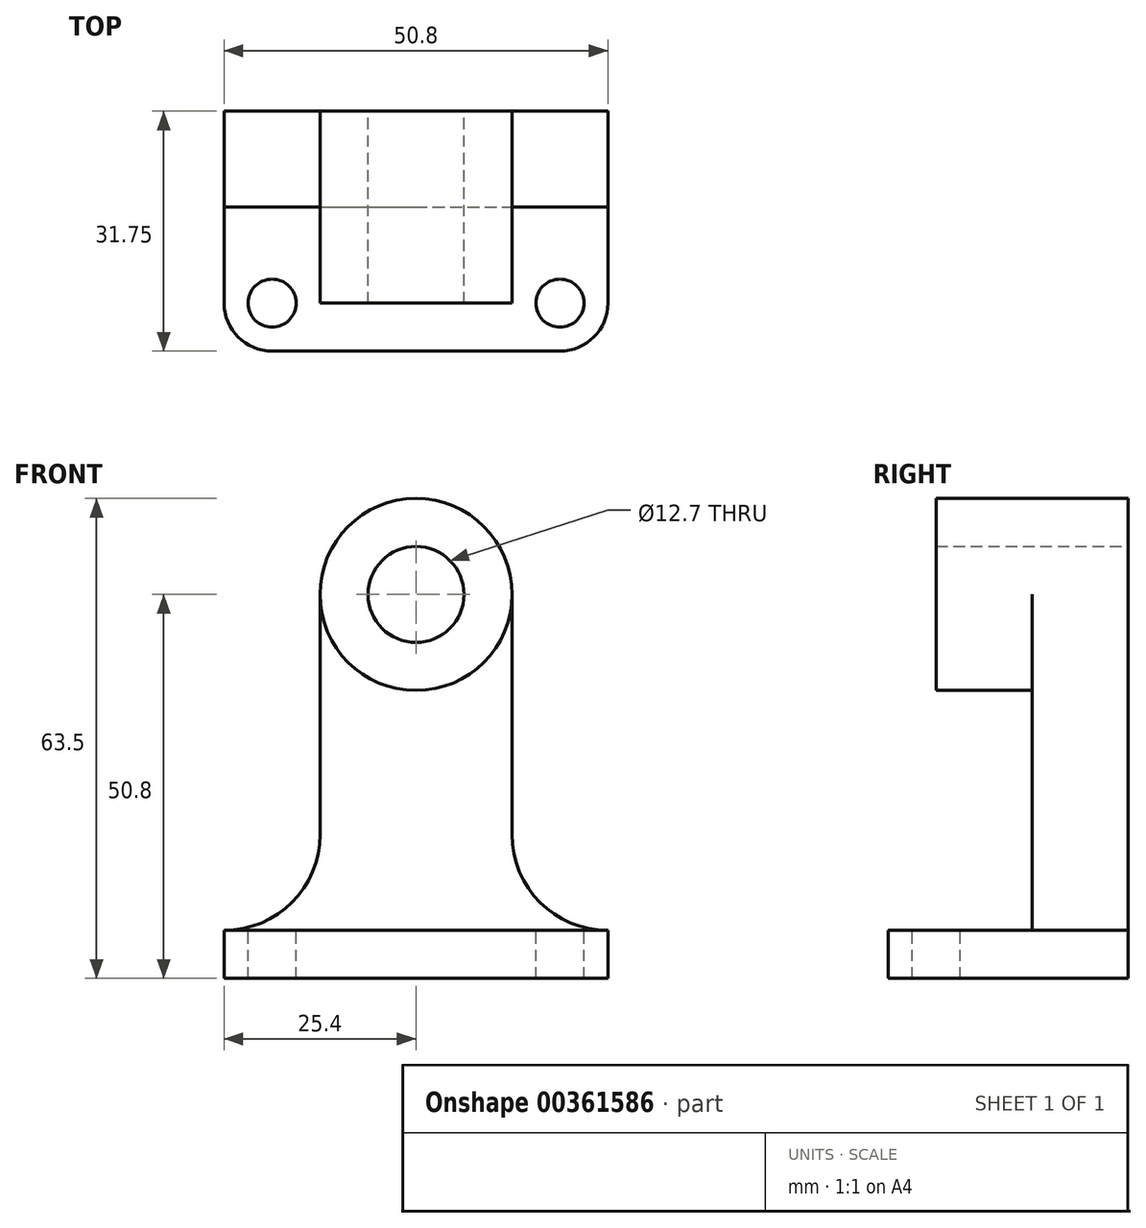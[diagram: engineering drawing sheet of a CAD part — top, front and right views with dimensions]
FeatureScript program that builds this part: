
annotation { "Feature Type Name" : "Feature", "Feature Type Description" : "" }
export const myFeature = defineFeature(function(context is Context, id is Id, definition is map)
    precondition{}
    {
        {
            var Q0;
            Q0=qCreatedBy(makeId("Front.planeOp"),FACE);
            var sketch = newSketch(context, id + "F0", { "sketchPlane" : qUnion([Q0])});
            skLineSegment(sketch, "E0", {"start": v(0, 0) * mm, "end": v(50.8, 0) * mm});
            skLineSegment(sketch, "E1", {"start": v(50.8, 0) * mm, "end": v(50.8, 63.5) * mm});
            skLineSegment(sketch, "E2", {"start": v(50.8, 63.5) * mm, "end": v(0, 63.5) * mm});
            skLineSegment(sketch, "E3", {"start": v(0, 63.5) * mm, "end": v(0, 0) * mm});
            skSolve(sketch);
        }
        {
            var Q0;
            Q0=makeQuery(id+"F0.imprint","IMPRINT",FACE,{"disambiguationData":[TD([[makeQuery(id+"F0.imprint","IMPRINT",EDGE,{"derivedFrom":sQuery(id+"F0.wireOp",EDGE,"E0")}),1.0]])]});
            extrude(context, id + "F1", {"entities" : qUnion([Q0]), "depth" : 31.75 * mm});
        }
        {
            var Q0;
            Q0=makeQuery(id+"F1.opExtrude","CAP_FACE",FACE,{"disambiguationData":[OSD([sQuery(id+"F0.wireOp",EDGE,"E0"),sQuery(id+"F0.wireOp",EDGE,"E1"),sQuery(id+"F0.wireOp",EDGE,"E2"),sQuery(id+"F0.wireOp",EDGE,"E3")])],"isStart":false});
            var sketch = newSketch(context, id + "F2", { "sketchPlane" : qUnion([Q0])});
            skLineSegment(sketch, "E4", {"start": v(0, 6.35) * mm, "end": v(50.8, 6.35) * mm});
            skLineSegment(sketch, "E5", {"start": v(12.7, 6.35) * mm, "end": v(12.7, 63.5) * mm});
            skLineSegment(sketch, "E6", {"start": v(12.7, 63.5) * mm, "end": v(38.1, 63.5) * mm});
            skLineSegment(sketch, "E7", {"start": v(38.1, 63.5) * mm, "end": v(38.1, 6.35) * mm});
            skLineSegment(sketch, "E8", {"start": v(12.7, 38.1) * mm, "end": v(38.1, 38.1) * mm});
            skSolve(sketch);
        }
        {
            var Q0;
            {var subQ4=makeQuery(id+"F1.opExtrude","CAP_EDGE",EDGE,{"disambiguationData":[OSD([sQuery(id+"F0.wireOp",EDGE,"E3")])],"isStart":false});var subQ6=sQuery(id+"F2.wireOp",EDGE,"E4");var subQ7=makeQuery(id+"F2.imprint","INTERSECT",VERTEX,{"derivedFrom":[subQ4,subQ6]});Q0=makeQuery(id+"F2.imprint","IMPRINT",FACE,{"disambiguationData":[TD([[makeQuery(id+"F2.imprint","IMPRINT",EDGE,{"disambiguationData":[TD([[subQ7,-1.0]])],"derivedFrom":subQ6}),1.0]])]});}
            var Q1;
            {var subQ5=sQuery(id+"F2.wireOp",EDGE,"E8");Q1=makeQuery(id+"F2.imprint","IMPRINT",FACE,{"disambiguationData":[TD([[makeQuery(id+"F2.imprint","IMPRINT",EDGE,{"derivedFrom":subQ5}),-1.0]])]});}
            var Q2;
            {var subQ1=makeQuery(id+"F1.opExtrude","CAP_EDGE",EDGE,{"disambiguationData":[OSD([sQuery(id+"F0.wireOp",EDGE,"E1")])],"isStart":false});var subQ3=sQuery(id+"F2.wireOp",EDGE,"E4");var subQ4=makeQuery(id+"F2.imprint","INTERSECT",VERTEX,{"derivedFrom":[subQ1,subQ3]});Q2=makeQuery(id+"F2.imprint","IMPRINT",FACE,{"disambiguationData":[TD([[makeQuery(id+"F2.imprint","IMPRINT",EDGE,{"disambiguationData":[TD([[subQ4,1.0]])],"derivedFrom":subQ3}),1.0]])]});}
            extrude(context, id + "F3", {"entities" : qUnion([Q0, Q1, Q2]), "operationType" : NewBodyOperationType.REMOVE, "oppositeDirection" : true, "depth" : 19.05 * mm});
        }
        {
            var Q0;
            {var subQ0=sQuery(id+"F0.wireOp",EDGE,"E2");Q0=makeQuery(id+"F3.boolean.opBoolean","SPLIT",FACE,{"disambiguationData":[TD([makeQuery(id+"F1.opExtrude","SWEPT_FACE",FACE,{"disambiguationData":[OSD([subQ0])]})])],"derivedFrom":makeQuery(id+"F1.opExtrude","CAP_FACE",FACE,{"disambiguationData":[OSD([sQuery(id+"F0.wireOp",EDGE,"E0"),sQuery(id+"F0.wireOp",EDGE,"E1"),subQ0,sQuery(id+"F0.wireOp",EDGE,"E3")])],"isStart":false})});}
            var sketch = newSketch(context, id + "F4", { "sketchPlane" : qUnion([Q0])});
            skCircle(sketch, "E9", {"center": v(25.4, 50.8) * mm, "radius": 12.7 * mm});
            skPoint(sketch, "E9.centerSnap0", {"position": v(38.1, 50.8) * mm});
            skSolve(sketch);
        }
        {
            var Q0;
            {var subQ0=sQuery(id+"F4.wireOp",EDGE,"E9");var subQ1=makeQuery(id+"F1.opExtrude","CAP_EDGE",EDGE,{"disambiguationData":[OSD([sQuery(id+"F0.wireOp",EDGE,"E2")])],"isStart":false});var subQ2=makeQuery(id+"F4.imprint","INTERSECT",VERTEX,{"derivedFrom":[subQ1,subQ0]});Q0=makeQuery(id+"F4.imprint","IMPRINT",FACE,{"disambiguationData":[TD([[makeQuery(id+"F4.imprint","IMPRINT",EDGE,{"disambiguationData":[TD([[subQ2,-1.0]])],"derivedFrom":subQ0}),-1.0]])]});}
            var Q1;
            {var subQ0=sQuery(id+"F4.wireOp",EDGE,"E9");var subQ1=makeQuery(id+"F1.opExtrude","CAP_EDGE",EDGE,{"disambiguationData":[OSD([sQuery(id+"F0.wireOp",EDGE,"E2")])],"isStart":false});var subQ2=makeQuery(id+"F4.imprint","INTERSECT",VERTEX,{"derivedFrom":[subQ1,subQ0]});Q1=makeQuery(id+"F4.imprint","IMPRINT",FACE,{"disambiguationData":[TD([[makeQuery(id+"F4.imprint","IMPRINT",EDGE,{"disambiguationData":[TD([[subQ2,1.0]])],"derivedFrom":subQ0}),-1.0]])]});}
            var Q2;
            {var subQ0=sQuery(id+"F4.wireOp",EDGE,"E9");var subQ1=makeQuery(id+"F3.boolean.opBoolean","COPY",EDGE,{"derivedFrom":makeQuery(id+"F3.opExtrude","CAP_EDGE",EDGE,{"disambiguationData":[OSD([sQuery(id+"F2.wireOp",EDGE,"E5")])],"isStart":true})});var subQ2=makeQuery(id+"F4.imprint","INTERSECT",VERTEX,{"derivedFrom":[subQ1,subQ0]});Q2=makeQuery(id+"F4.imprint","IMPRINT",FACE,{"disambiguationData":[TD([[makeQuery(id+"F4.imprint","IMPRINT",EDGE,{"disambiguationData":[TD([[subQ2,-1.0]])],"derivedFrom":subQ0}),-1.0]])]});}
            var Q3;
            {var subQ0=sQuery(id+"F4.wireOp",EDGE,"E9");var subQ1=makeQuery(id+"F3.boolean.opBoolean","COPY",EDGE,{"derivedFrom":makeQuery(id+"F3.opExtrude","CAP_EDGE",EDGE,{"disambiguationData":[OSD([sQuery(id+"F2.wireOp",EDGE,"E7")])],"isStart":true})});var subQ2=makeQuery(id+"F4.imprint","INTERSECT",VERTEX,{"derivedFrom":[subQ1,subQ0]});Q3=makeQuery(id+"F4.imprint","IMPRINT",FACE,{"disambiguationData":[TD([[makeQuery(id+"F4.imprint","IMPRINT",EDGE,{"disambiguationData":[TD([[subQ2,1.0]])],"derivedFrom":subQ0}),-1.0]])]});}
            extrude(context, id + "F5", {"entities" : qUnion([Q0, Q1, Q2, Q3]), "operationType" : NewBodyOperationType.REMOVE, "oppositeDirection" : true, "depth" : 19.05 * mm});
        }
        {
            var Q0;
            {var subQ0=sQuery(id+"F0.wireOp",EDGE,"E2");Q0=makeQuery(id+"F3.boolean.opBoolean","SPLIT",FACE,{"disambiguationData":[TD([makeQuery(id+"F1.opExtrude","SWEPT_FACE",FACE,{"disambiguationData":[OSD([subQ0])]})])],"derivedFrom":makeQuery(id+"F1.opExtrude","CAP_FACE",FACE,{"disambiguationData":[OSD([sQuery(id+"F0.wireOp",EDGE,"E0"),sQuery(id+"F0.wireOp",EDGE,"E1"),subQ0,sQuery(id+"F0.wireOp",EDGE,"E3")])],"isStart":false})});}
            extrude(context, id + "F6", {"entities" : qUnion([Q0]), "operationType" : NewBodyOperationType.REMOVE, "oppositeDirection" : true, "depth" : 6.35 * mm});
        }
        {
            var Q0;
            {var subQ0=sQuery(id+"F4.wireOp",EDGE,"E9");var subQ1=sQuery(id+"F2.wireOp",EDGE,"E8");var subQ2=sQuery(id+"F2.wireOp",EDGE,"E7");var subQ3=sQuery(id+"F2.wireOp",EDGE,"E5");var subQ4=sQuery(id+"F0.wireOp",EDGE,"E2");Q0=makeQuery(id+"F5.boolean.opBoolean","MERGE",FACE,{"derivedFrom":[makeQuery(id+"F3.boolean.opBoolean","COPY",FACE,{"derivedFrom":makeQuery(id+"F3.opExtrude","CAP_FACE",FACE,{"disambiguationData":[OSD([sQuery(id+"F0.wireOp",EDGE,"E1"),subQ4,sQuery(id+"F0.wireOp",EDGE,"E3"),sQuery(id+"F2.wireOp",EDGE,"E4"),subQ3,subQ2,subQ1])],"isStart":false})}),makeQuery(id+"F5.opExtrude","CAP_FACE",FACE,{"disambiguationData":[OSD([subQ4,subQ2,subQ0])],"isStart":false}),makeQuery(id+"F5.opExtrude","CAP_FACE",FACE,{"disambiguationData":[OSD([subQ4,subQ3,subQ0])],"isStart":false}),makeQuery(id+"F5.opExtrude","CAP_FACE",FACE,{"disambiguationData":[OSD([subQ3,subQ1,subQ0])],"isStart":false}),makeQuery(id+"F5.opExtrude","CAP_FACE",FACE,{"disambiguationData":[OSD([subQ2,subQ1,subQ0])],"isStart":false})]});}
            var sketch = newSketch(context, id + "F7", { "sketchPlane" : qUnion([Q0])});
            skLineSegment(sketch, "E10", {"start": v(38.1, 63.5) * mm, "end": v(38.1, 6.35) * mm});
            skLineSegment(sketch, "E11", {"start": v(12.7, 63.5) * mm, "end": v(12.7, 6.35) * mm});
            skCircle(sketch, "E12", {"center": v(0, 19.05) * mm, "radius": 12.7 * mm});
            skCircle(sketch, "E13", {"center": v(50.8, 19.05) * mm, "radius": 12.7 * mm});
            skSolve(sketch);
        }
        {
            var Q0;
            {var subQ0=sQuery(id+"F7.wireOp",EDGE,"E12");var subQ1=makeQuery(id+"F7.imprint","INTERSECT",VERTEX,{"derivedFrom":[sQuery(id+"F7.wireOp",EDGE,"E11"),subQ0]});Q0=makeQuery(id+"F7.imprint","IMPRINT",FACE,{"disambiguationData":[TD([[makeQuery(id+"F7.imprint","IMPRINT",EDGE,{"disambiguationData":[TD([[subQ1,-1.0]])],"derivedFrom":subQ0}),1.0]])]});}
            var Q1;
            {var subQ11=sQuery(id+"F7.wireOp",EDGE,"E12");var subQ13=sQuery(id+"F7.wireOp",EDGE,"E11");var subQ14=makeQuery(id+"F7.imprint","INTERSECT",VERTEX,{"derivedFrom":[subQ13,subQ11]});Q1=makeQuery(id+"F7.imprint","IMPRINT",FACE,{"disambiguationData":[TD([[makeQuery(id+"F7.imprint","IMPRINT",EDGE,{"disambiguationData":[TD([[subQ14,-1.0]])],"derivedFrom":subQ11}),-1.0]])]});}
            var Q2;
            {var subQ0=sQuery(id+"F7.wireOp",EDGE,"E13");var subQ1=sQuery(id+"F7.wireOp",EDGE,"E10");var subQ2=makeQuery(id+"F7.imprint","INTERSECT",VERTEX,{"derivedFrom":[subQ1,subQ0]});Q2=makeQuery(id+"F7.imprint","IMPRINT",FACE,{"disambiguationData":[TD([[makeQuery(id+"F7.imprint","IMPRINT",EDGE,{"disambiguationData":[TD([[subQ2,1.0]])],"derivedFrom":subQ0}),-1.0]])]});}
            var Q3;
            {var subQ0=sQuery(id+"F7.wireOp",EDGE,"E13");var subQ1=makeQuery(id+"F7.imprint","INTERSECT",VERTEX,{"derivedFrom":[sQuery(id+"F7.wireOp",EDGE,"E10"),subQ0]});Q3=makeQuery(id+"F7.imprint","IMPRINT",FACE,{"disambiguationData":[TD([[makeQuery(id+"F7.imprint","IMPRINT",EDGE,{"disambiguationData":[TD([[subQ1,1.0]])],"derivedFrom":subQ0}),1.0]])]});}
            extrude(context, id + "F8", {"entities" : qUnion([Q0, Q1, Q2, Q3]), "operationType" : NewBodyOperationType.REMOVE, "oppositeDirection" : true, "depth" : 25.4 * mm});
        }
        {
            var Q0;
            {var subQ0=sQuery(id+"F4.wireOp",EDGE,"E9");var subQ1=sQuery(id+"F2.wireOp",EDGE,"E5");var subQ2=sQuery(id+"F0.wireOp",EDGE,"E2");var subQ3=makeQuery(id+"F5.opExtrude","CAP_FACE",FACE,{"disambiguationData":[OSD([subQ2,subQ1,subQ0])],"isStart":false});var subQ4=sQuery(id+"F2.wireOp",EDGE,"E7");var subQ5=makeQuery(id+"F4.imprint","INTERSECT",VERTEX,{"derivedFrom":[makeQuery(id+"F3.boolean.opBoolean","COPY",EDGE,{"derivedFrom":makeQuery(id+"F3.opExtrude","CAP_EDGE",EDGE,{"disambiguationData":[OSD([subQ4])],"isStart":true})}),subQ0]});var subQ6=sQuery(id+"F2.wireOp",EDGE,"E8");var subQ8=makeQuery(id+"F4.imprint","INTERSECT",VERTEX,{"derivedFrom":[makeQuery(id+"F3.boolean.opBoolean","COPY",EDGE,{"derivedFrom":makeQuery(id+"F3.opExtrude","CAP_EDGE",EDGE,{"disambiguationData":[OSD([subQ1])],"isStart":true})}),subQ0]});var subQ9=makeQuery(id+"F4.imprint","INTERSECT",VERTEX,{"derivedFrom":[makeQuery(id+"F1.opExtrude","CAP_EDGE",EDGE,{"disambiguationData":[OSD([subQ2])],"isStart":false}),subQ0]});var subQ10=makeQuery(id+"F3.boolean.opBoolean","COPY",FACE,{"derivedFrom":makeQuery(id+"F3.opExtrude","CAP_FACE",FACE,{"disambiguationData":[OSD([sQuery(id+"F0.wireOp",EDGE,"E1"),subQ2,sQuery(id+"F0.wireOp",EDGE,"E3"),sQuery(id+"F2.wireOp",EDGE,"E4"),subQ1,subQ4,subQ6])],"isStart":false})});var subQ11=makeQuery(id+"F5.opExtrude","CAP_FACE",FACE,{"disambiguationData":[OSD([subQ4,subQ6,subQ0])],"isStart":false});var subQ12=makeQuery(id+"F5.opExtrude","CAP_FACE",FACE,{"disambiguationData":[OSD([subQ2,subQ4,subQ0])],"isStart":false});var subQ13=makeQuery(id+"F5.opExtrude","CAP_FACE",FACE,{"disambiguationData":[OSD([subQ1,subQ6,subQ0])],"isStart":false});Q0=makeQuery(id+"F8.boolean.opBoolean","SPLIT",FACE,{"disambiguationData":[TD([makeQuery(id+"F1.opExtrude","SWEPT_FACE",FACE,{"disambiguationData":[OSD([subQ2])]}),subQ10,subQ12,subQ3,subQ13,subQ11,makeQuery(id+"F5.boolean.opBoolean","TWEAK_FACE",FACE,{"derivedFrom":[makeQuery(id+"F5.opExtrude","SWEPT_FACE",FACE,{"disambiguationData":[OSD([subQ0]),TDD([makeQuery(id+"F4.imprint","IMPRINT",EDGE,{"disambiguationData":[TD([[subQ9,1.0]])],"derivedFrom":subQ0})])]}),makeQuery(id+"F5.opExtrude","SWEPT_FACE",FACE,{"disambiguationData":[OSD([subQ0]),TDD([makeQuery(id+"F4.imprint","IMPRINT",EDGE,{"disambiguationData":[TD([[subQ9,-1.0]])],"derivedFrom":subQ0})])]}),makeQuery(id+"F5.opExtrude","SWEPT_FACE",FACE,{"disambiguationData":[OSD([subQ0]),TDD([makeQuery(id+"F4.imprint","IMPRINT",EDGE,{"disambiguationData":[TD([[subQ8,-1.0]])],"derivedFrom":subQ0})])]}),makeQuery(id+"F5.opExtrude","SWEPT_FACE",FACE,{"disambiguationData":[OSD([subQ0]),TDD([makeQuery(id+"F4.imprint","IMPRINT",EDGE,{"disambiguationData":[TD([[subQ5,1.0]])],"derivedFrom":subQ0})])]})]}),makeQuery(id+"F8.opExtrude","SWEPT_FACE",FACE,{"disambiguationData":[OSD([sQuery(id+"F7.wireOp",EDGE,"E11")])]})])],"derivedFrom":makeQuery(id+"F5.boolean.opBoolean","MERGE",FACE,{"derivedFrom":[subQ10,subQ12,subQ3,subQ13,subQ11]})});}
            var Q1;
            {var subQ0=sQuery(id+"F4.wireOp",EDGE,"E9");var subQ1=sQuery(id+"F2.wireOp",EDGE,"E5");var subQ2=sQuery(id+"F0.wireOp",EDGE,"E2");var subQ3=makeQuery(id+"F5.opExtrude","CAP_FACE",FACE,{"disambiguationData":[OSD([subQ2,subQ1,subQ0])],"isStart":false});var subQ4=sQuery(id+"F2.wireOp",EDGE,"E7");var subQ5=makeQuery(id+"F4.imprint","INTERSECT",VERTEX,{"derivedFrom":[makeQuery(id+"F3.boolean.opBoolean","COPY",EDGE,{"derivedFrom":makeQuery(id+"F3.opExtrude","CAP_EDGE",EDGE,{"disambiguationData":[OSD([subQ4])],"isStart":true})}),subQ0]});var subQ6=sQuery(id+"F2.wireOp",EDGE,"E8");var subQ8=makeQuery(id+"F4.imprint","INTERSECT",VERTEX,{"derivedFrom":[makeQuery(id+"F3.boolean.opBoolean","COPY",EDGE,{"derivedFrom":makeQuery(id+"F3.opExtrude","CAP_EDGE",EDGE,{"disambiguationData":[OSD([subQ1])],"isStart":true})}),subQ0]});var subQ9=makeQuery(id+"F4.imprint","INTERSECT",VERTEX,{"derivedFrom":[makeQuery(id+"F1.opExtrude","CAP_EDGE",EDGE,{"disambiguationData":[OSD([subQ2])],"isStart":false}),subQ0]});var subQ10=makeQuery(id+"F3.boolean.opBoolean","COPY",FACE,{"derivedFrom":makeQuery(id+"F3.opExtrude","CAP_FACE",FACE,{"disambiguationData":[OSD([sQuery(id+"F0.wireOp",EDGE,"E1"),subQ2,sQuery(id+"F0.wireOp",EDGE,"E3"),sQuery(id+"F2.wireOp",EDGE,"E4"),subQ1,subQ4,subQ6])],"isStart":false})});var subQ11=makeQuery(id+"F5.opExtrude","CAP_FACE",FACE,{"disambiguationData":[OSD([subQ4,subQ6,subQ0])],"isStart":false});var subQ12=makeQuery(id+"F5.opExtrude","CAP_FACE",FACE,{"disambiguationData":[OSD([subQ2,subQ4,subQ0])],"isStart":false});var subQ13=makeQuery(id+"F5.opExtrude","CAP_FACE",FACE,{"disambiguationData":[OSD([subQ1,subQ6,subQ0])],"isStart":false});Q1=makeQuery(id+"F8.boolean.opBoolean","SPLIT",FACE,{"disambiguationData":[TD([makeQuery(id+"F1.opExtrude","SWEPT_FACE",FACE,{"disambiguationData":[OSD([subQ2])]}),subQ10,subQ12,subQ3,subQ13,subQ11,makeQuery(id+"F5.boolean.opBoolean","TWEAK_FACE",FACE,{"derivedFrom":[makeQuery(id+"F5.opExtrude","SWEPT_FACE",FACE,{"disambiguationData":[OSD([subQ0]),TDD([makeQuery(id+"F4.imprint","IMPRINT",EDGE,{"disambiguationData":[TD([[subQ9,1.0]])],"derivedFrom":subQ0})])]}),makeQuery(id+"F5.opExtrude","SWEPT_FACE",FACE,{"disambiguationData":[OSD([subQ0]),TDD([makeQuery(id+"F4.imprint","IMPRINT",EDGE,{"disambiguationData":[TD([[subQ9,-1.0]])],"derivedFrom":subQ0})])]}),makeQuery(id+"F5.opExtrude","SWEPT_FACE",FACE,{"disambiguationData":[OSD([subQ0]),TDD([makeQuery(id+"F4.imprint","IMPRINT",EDGE,{"disambiguationData":[TD([[subQ8,-1.0]])],"derivedFrom":subQ0})])]}),makeQuery(id+"F5.opExtrude","SWEPT_FACE",FACE,{"disambiguationData":[OSD([subQ0]),TDD([makeQuery(id+"F4.imprint","IMPRINT",EDGE,{"disambiguationData":[TD([[subQ5,1.0]])],"derivedFrom":subQ0})])]})]}),makeQuery(id+"F8.opExtrude","SWEPT_FACE",FACE,{"disambiguationData":[OSD([sQuery(id+"F7.wireOp",EDGE,"E10")])]})])],"derivedFrom":makeQuery(id+"F5.boolean.opBoolean","MERGE",FACE,{"derivedFrom":[subQ10,subQ12,subQ3,subQ13,subQ11]})});}
            extrude(context, id + "F9", {"entities" : qUnion([Q0, Q1]), "operationType" : NewBodyOperationType.REMOVE, "oppositeDirection" : true, "depth" : 25.4 * mm});
        }
        {
            var Q0;
            Q0=makeQuery(id+"F3.boolean.opBoolean","COPY",FACE,{"derivedFrom":makeQuery(id+"F3.opExtrude","SWEPT_FACE",FACE,{"disambiguationData":[OSD([sQuery(id+"F2.wireOp",EDGE,"E4")])]})});
            var sketch = newSketch(context, id + "F10", { "sketchPlane" : qUnion([Q0])});
            skCircle(sketch, "E14", {"center": v(44.45, -25.4) * mm, "radius": 6.35 * mm});
            skCircle(sketch, "E15", {"center": v(6.35, -25.4) * mm, "radius": 6.35 * mm});
            skSolve(sketch);
        }
        {
            var Q0;
            {var subQ0=sQuery(id+"F10.wireOp",EDGE,"E15");var subQ1=sQuery(id+"F2.wireOp",EDGE,"E4");var subQ4=makeQuery(id+"F3.boolean.opBoolean","COPY",EDGE,{"derivedFrom":makeQuery(id+"F3.opExtrude","CAP_EDGE",EDGE,{"disambiguationData":[OSD([subQ1])],"isStart":true})});var subQ5=makeQuery(id+"F10.imprint","INTERSECT",VERTEX,{"derivedFrom":[subQ4,subQ0]});Q0=makeQuery(id+"F10.imprint","IMPRINT",FACE,{"disambiguationData":[TD([[makeQuery(id+"F10.imprint","IMPRINT",EDGE,{"disambiguationData":[TD([[subQ5,1.0]])],"derivedFrom":subQ0}),-1.0]])]});}
            var Q1;
            {var subQ0=sQuery(id+"F10.wireOp",EDGE,"E14");var subQ1=sQuery(id+"F2.wireOp",EDGE,"E4");var subQ4=makeQuery(id+"F3.boolean.opBoolean","COPY",EDGE,{"derivedFrom":makeQuery(id+"F3.opExtrude","CAP_EDGE",EDGE,{"disambiguationData":[OSD([subQ1])],"isStart":true})});var subQ5=makeQuery(id+"F10.imprint","INTERSECT",VERTEX,{"derivedFrom":[subQ4,subQ0]});Q1=makeQuery(id+"F10.imprint","IMPRINT",FACE,{"disambiguationData":[TD([[makeQuery(id+"F10.imprint","IMPRINT",EDGE,{"disambiguationData":[TD([[subQ5,-1.0]])],"derivedFrom":subQ0}),-1.0]])]});}
            extrude(context, id + "F11", {"entities" : qUnion([Q0, Q1]), "operationType" : NewBodyOperationType.REMOVE, "oppositeDirection" : true, "depth" : 6.35 * mm});
        }
        {
            var Q0;
            Q0=makeQuery(id+"F3.boolean.opBoolean","COPY",FACE,{"derivedFrom":makeQuery(id+"F3.opExtrude","SWEPT_FACE",FACE,{"disambiguationData":[OSD([sQuery(id+"F2.wireOp",EDGE,"E4")])]})});
            var sketch = newSketch(context, id + "F12", { "sketchPlane" : qUnion([Q0])});
            skCircle(sketch, "E16", {"center": v(44.45, -25.4) * mm, "radius": 3.18 * mm});
            skCircle(sketch, "E17", {"center": v(6.35, -25.4) * mm, "radius": 3.18 * mm});
            skSolve(sketch);
        }
        {
            var Q0;
            Q0=makeQuery(id+"F12.imprint","IMPRINT",FACE,{"disambiguationData":[TD([[makeQuery(id+"F12.imprint","IMPRINT",EDGE,{"derivedFrom":sQuery(id+"F12.wireOp",EDGE,"E17")}),1.0]])]});
            var Q1;
            Q1=makeQuery(id+"F12.imprint","IMPRINT",FACE,{"disambiguationData":[TD([[makeQuery(id+"F12.imprint","IMPRINT",EDGE,{"derivedFrom":sQuery(id+"F12.wireOp",EDGE,"E16")}),1.0]])]});
            extrude(context, id + "F13", {"entities" : qUnion([Q0, Q1]), "operationType" : NewBodyOperationType.REMOVE, "oppositeDirection" : true, "depth" : 6.35 * mm});
        }
        {
            var Q0;
            Q0=makeQuery(id+"F1.opExtrude","CAP_FACE",FACE,{"disambiguationData":[OSD([sQuery(id+"F0.wireOp",EDGE,"E0"),sQuery(id+"F0.wireOp",EDGE,"E1"),sQuery(id+"F0.wireOp",EDGE,"E2"),sQuery(id+"F0.wireOp",EDGE,"E3")])],"isStart":true});
            var sketch = newSketch(context, id + "F14", { "sketchPlane" : qUnion([Q0])});
            skCircle(sketch, "E18", {"center": v(-25.4, 50.8) * mm, "radius": 6.35 * mm});
            skSolve(sketch);
        }
        {
            var Q0;
            Q0=makeQuery(id+"F14.imprint","IMPRINT",FACE,{"disambiguationData":[TD([[makeQuery(id+"F14.imprint","IMPRINT",EDGE,{"derivedFrom":sQuery(id+"F14.wireOp",EDGE,"E18")}),1.0]])]});
            extrude(context, id + "F15", {"entities" : qUnion([Q0]), "operationType" : NewBodyOperationType.REMOVE, "oppositeDirection" : true, "depth" : 25.4 * mm});
        }
    });
